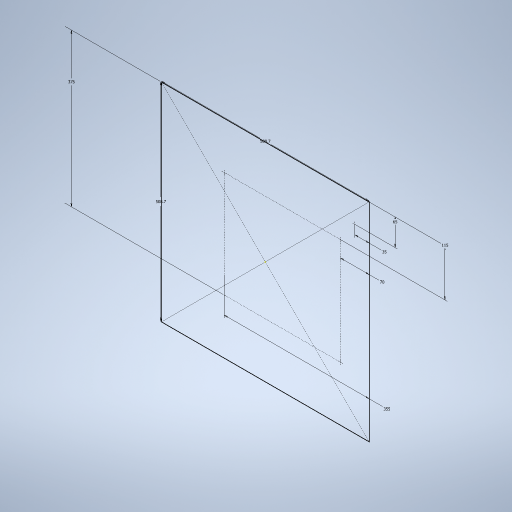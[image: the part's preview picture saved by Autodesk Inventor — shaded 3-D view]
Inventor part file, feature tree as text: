
AUTODESK INVENTOR PART (.ipt)
format: ipt  version: 2024 (Build 280153000, 153)  size: 243,200 bytes
history: native  units: mm
features: sketch x1
ambient origin geometry x8: Origin, YZ Plane, XZ Plane, XY Plane, X Axis, Y Axis, Z Axis, Center Point
feature tree (1):
  sketch  "Sketch1"  dims[d0=508.7mm d1=508.7mm d2=35.0mm d3=65.0mm d4=70.0mm d5=115.0mm d6=355.0mm d7=375.0mm]
